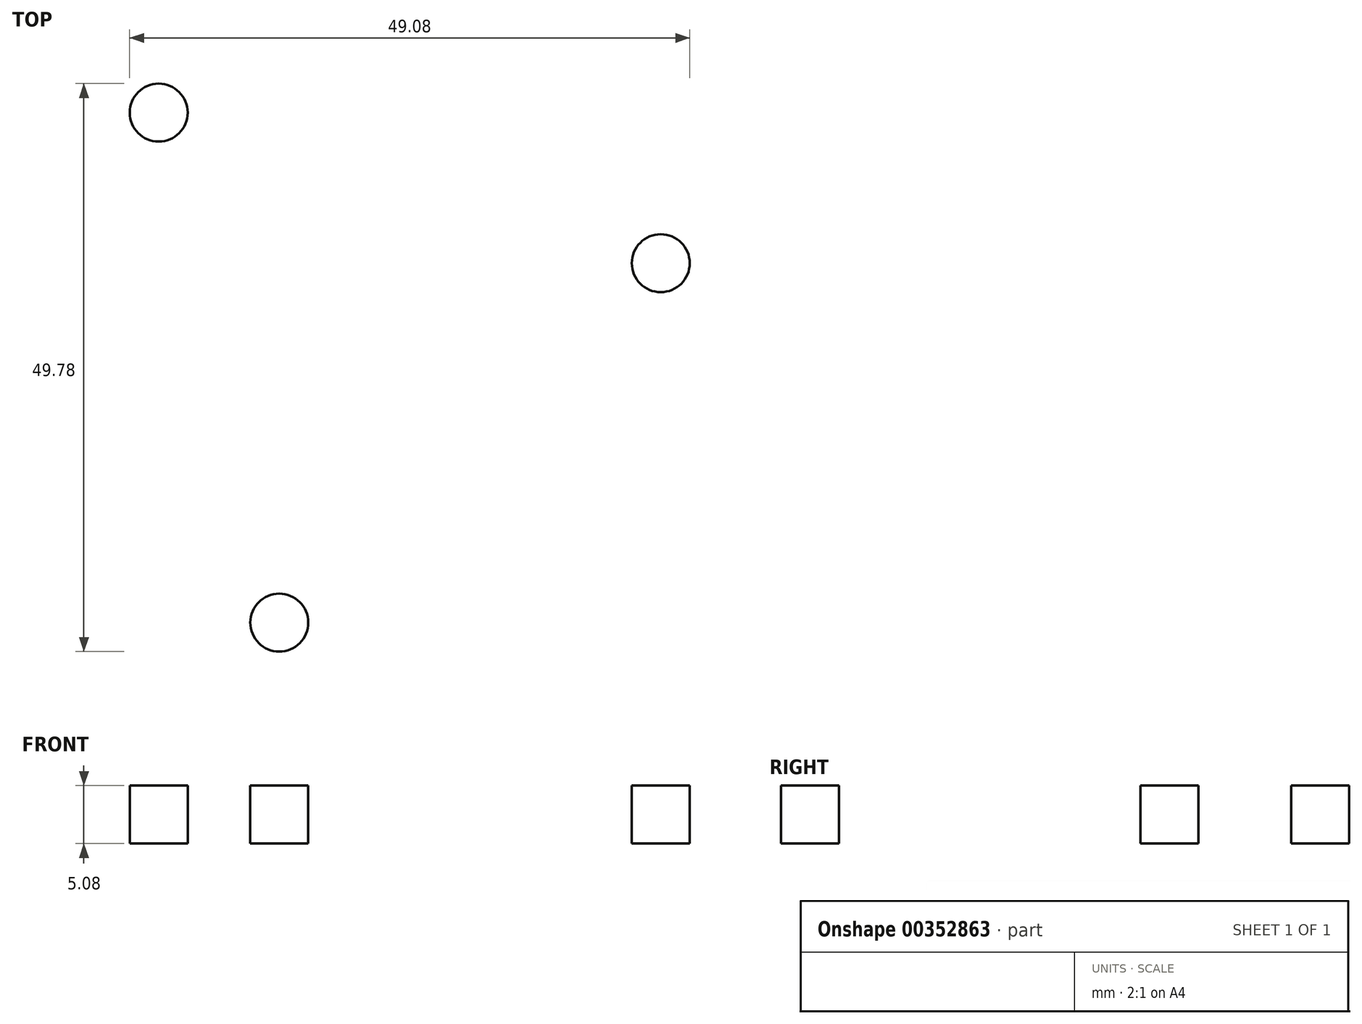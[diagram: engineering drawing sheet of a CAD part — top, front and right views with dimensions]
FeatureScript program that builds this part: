
annotation { "Feature Type Name" : "Feature", "Feature Type Description" : "" }
export const myFeature = defineFeature(function(context is Context, id is Id, definition is map)
    precondition{}
    {
        {
            var Q0;
            Q0=qCreatedBy(makeId("Top.planeOp"),FACE);
            var sketch = newSketch(context, id + "F0", { "sketchPlane" : qUnion([Q0])});
            skArc(sketch, "E0", {"start": v(-18.45, 33.34) * mm, "mid": v(-33, 19.05) * mm, "end": v(-38.1, -0.7) * mm});
            skArc(sketch, "E1", {"start": v(-18.45, 33.34) * mm, "mid": v(0, 25.4) * mm, "end": v(18.45, 33.34) * mm});
            skArc(sketch, "E2.1.0", {"start": v(-19.65, -32.64) * mm, "mid": v(-22, -12.7) * mm, "end": v(-38.1, -0.7) * mm});
            skArc(sketch, "E2.2.0", {"start": v(38.1, -0.7) * mm, "mid": v(22, -12.7) * mm, "end": v(19.65, -32.64) * mm});
            skArc(sketch, "E3.trimOffspring", {"start": v(-19.65, -32.64) * mm, "mid": v(0, -38.1) * mm, "end": v(19.65, -32.64) * mm});
            skArc(sketch, "E4.trimOffspring", {"start": v(38.1, -0.7) * mm, "mid": v(33, 19.05) * mm, "end": v(18.45, 33.34) * mm});
            skSolve(sketch);
        }
        {
            var Q0;
            Q0=makeQuery(id+"F0.imprint","IMPRINT",FACE,{"disambiguationData":[TD([[makeQuery(id+"F0.imprint","IMPRINT",EDGE,{"derivedFrom":sQuery(id+"F0.wireOp",EDGE,"E0")}),1.0]])]});
            extrude(context, id + "F1", {"entities" : qUnion([Q0]), "depth" : 5.08 * mm});
        }
        {
            var Q0;
            Q0=makeQuery(id+"F1.opExtrude","CAP_FACE",FACE,{"disambiguationData":[OSD([sQuery(id+"F0.wireOp",EDGE,"E0"),sQuery(id+"F0.wireOp",EDGE,"E1"),sQuery(id+"F0.wireOp",EDGE,"E2.1.0"),sQuery(id+"F0.wireOp",EDGE,"E2.2.0"),sQuery(id+"F0.wireOp",EDGE,"E3.trimOffspring"),sQuery(id+"F0.wireOp",EDGE,"E4.trimOffspring")])],"isStart":false});
            var sketch = newSketch(context, id + "F2", { "sketchPlane" : qUnion([Q0])});
            skCircle(sketch, "E5", {"center": v(0, 0) * mm, "radius": 15.24 * mm});
            skCircle(sketch, "E6", {"center": v(7.62, -25.4) * mm, "radius": 2.54 * mm});
            skCircle(sketch, "E7.MirrorC", {"center": v(-7.62, -25.4) * mm, "radius": 2.54 * mm});
            skCircle(sketch, "E8.1.0", {"center": v(25.8, 6.1) * mm, "radius": 2.54 * mm});
            skCircle(sketch, "E8.1.1", {"center": v(18.19, 19.3) * mm, "radius": 2.54 * mm});
            skCircle(sketch, "E8.2.0", {"center": v(-18.19, 19.3) * mm, "radius": 2.54 * mm});
            skCircle(sketch, "E8.2.1", {"center": v(-25.8, 6.1) * mm, "radius": 2.54 * mm});
            skSolve(sketch);
        }
        {
            var Q0;
            Q0=makeQuery(id+"F2.imprint","IMPRINT",FACE,{"disambiguationData":[TD([[makeQuery(id+"F2.imprint","IMPRINT",EDGE,{"derivedFrom":sQuery(id+"F2.wireOp",EDGE,"E5")}),1.0]])]});
            extrude(context, id + "F3", {"entities" : qUnion([Q0]), "operationType" : NewBodyOperationType.REMOVE, "oppositeDirection" : true, "depth" : 25.4 * mm});
        }
        {
            var Q0;
            Q0=makeQuery(id+"F2.imprint","IMPRINT",FACE,{"disambiguationData":[TD([[makeQuery(id+"F2.imprint","IMPRINT",EDGE,{"derivedFrom":sQuery(id+"F2.wireOp",EDGE,"E6")}),1.0]])]});
            var Q1;
            Q1=makeQuery(id+"F2.imprint","IMPRINT",FACE,{"disambiguationData":[TD([[makeQuery(id+"F2.imprint","IMPRINT",EDGE,{"derivedFrom":sQuery(id+"F2.wireOp",EDGE,"E7.MirrorC")}),-1.0]])]});
            var Q2;
            Q2=makeQuery(id+"F2.imprint","IMPRINT",FACE,{"disambiguationData":[TD([[makeQuery(id+"F2.imprint","IMPRINT",EDGE,{"derivedFrom":sQuery(id+"F2.wireOp",EDGE,"E8.2.1")}),1.0]])]});
            var Q3;
            Q3=makeQuery(id+"F2.imprint","IMPRINT",FACE,{"disambiguationData":[TD([[makeQuery(id+"F2.imprint","IMPRINT",EDGE,{"derivedFrom":sQuery(id+"F2.wireOp",EDGE,"E8.2.0")}),-1.0]])]});
            var Q4;
            Q4=makeQuery(id+"F2.imprint","IMPRINT",FACE,{"disambiguationData":[TD([[makeQuery(id+"F2.imprint","IMPRINT",EDGE,{"derivedFrom":sQuery(id+"F2.wireOp",EDGE,"E8.1.1")}),1.0]])]});
            var Q5;
            Q5=makeQuery(id+"F2.imprint","IMPRINT",FACE,{"disambiguationData":[TD([[makeQuery(id+"F2.imprint","IMPRINT",EDGE,{"derivedFrom":sQuery(id+"F2.wireOp",EDGE,"E8.1.0")}),-1.0]])]});
            var Q6;
            Q6=sQuery(id+"F2.wireOp",EDGE,"E6");
            var Q7;
            Q7=sQuery(id+"F2.wireOp",EDGE,"E7.MirrorC");
            extrude(context, id + "F4", {"entities" : qUnion([Q0, Q1, Q2, Q3, Q4, Q5]), "operationType" : NewBodyOperationType.REMOVE, "surfaceEntities" : qUnion([Q6, Q7]), "oppositeDirection" : true, "depth" : 25.4 * mm});
        }
    });
